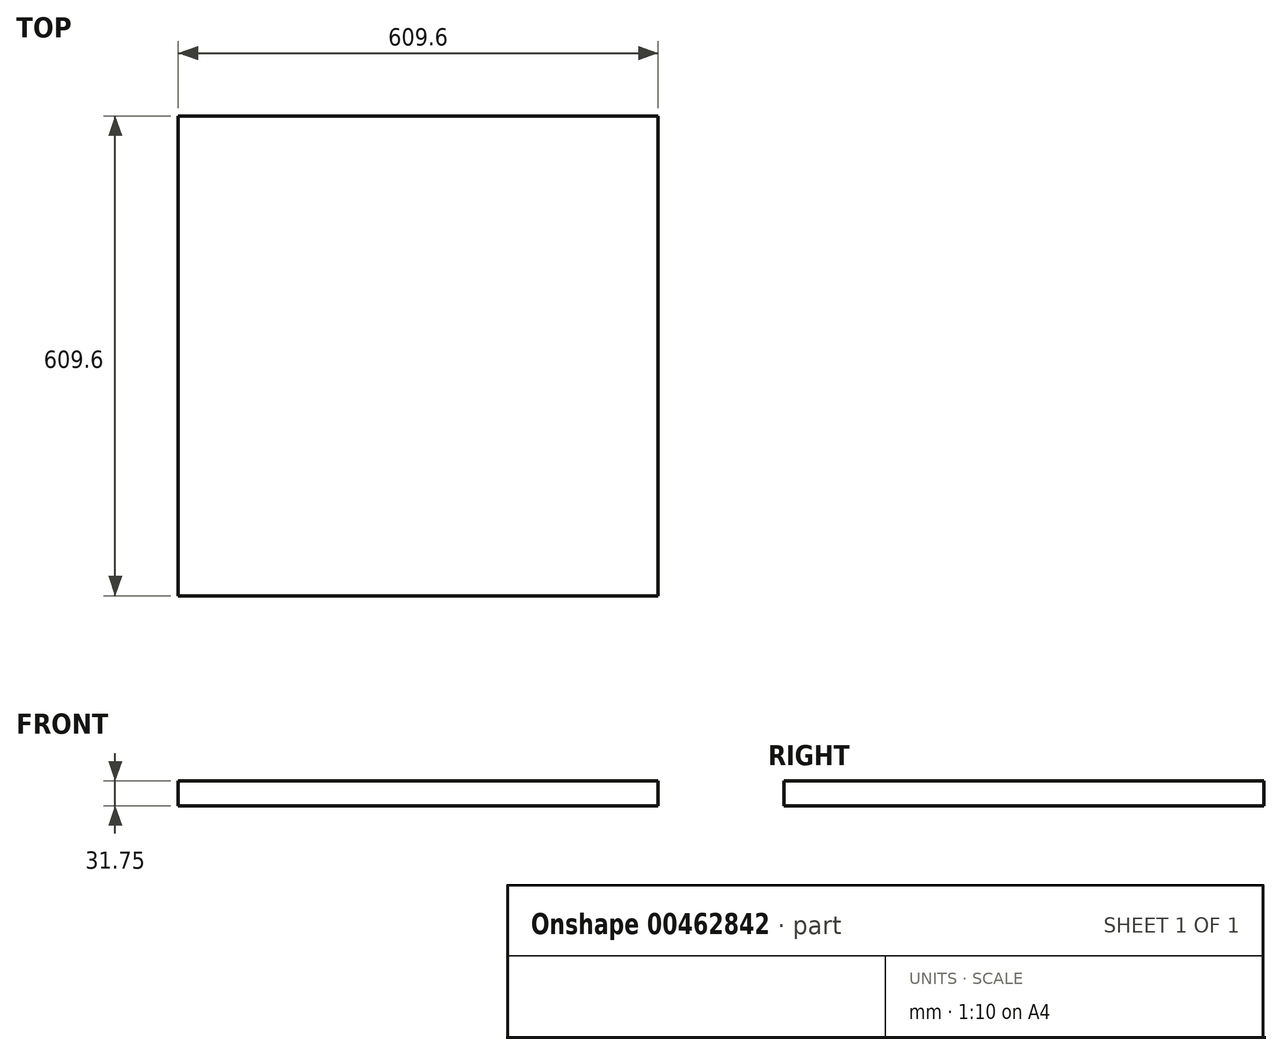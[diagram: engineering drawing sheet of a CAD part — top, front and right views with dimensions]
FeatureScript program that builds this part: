
annotation { "Feature Type Name" : "Feature", "Feature Type Description" : "" }
export const myFeature = defineFeature(function(context is Context, id is Id, definition is map)
    precondition{}
    {
        {
            var Q0;
            Q0=qCreatedBy(makeId("Top.planeOp"),FACE);
            var sketch = newSketch(context, id + "F0", { "sketchPlane" : qUnion([Q0])});
            skLineSegment(sketch, "E0.bottom", {"start": v(-304.8, -304.8) * mm, "end": v(304.8, -304.8) * mm});
            skLineSegment(sketch, "E0.top", {"start": v(-304.8, 304.8) * mm, "end": v(304.8, 304.8) * mm});
            skLineSegment(sketch, "E0.left", {"start": v(-304.8, -304.8) * mm, "end": v(-304.8, 304.8) * mm});
            skLineSegment(sketch, "E0.right", {"start": v(304.8, -304.8) * mm, "end": v(304.8, 304.8) * mm});
            skLineSegment(sketch, "E1", {"start": v(-304.8, -304.8) * mm, "end": v(304.8, 304.8) * mm, "construction": true});
            skSolve(sketch);
        }
        {
            var Q0;
            Q0=makeQuery(id+"F0.imprint","IMPRINT",FACE,{"disambiguationData":[TD([[makeQuery(id+"F0.imprint","IMPRINT",EDGE,{"derivedFrom":sQuery(id+"F0.wireOp",EDGE,"E0.bottom")}),1.0]])]});
            extrude(context, id + "F1", {"entities" : qUnion([Q0]), "depth" : 31.75 * mm});
        }
    });
